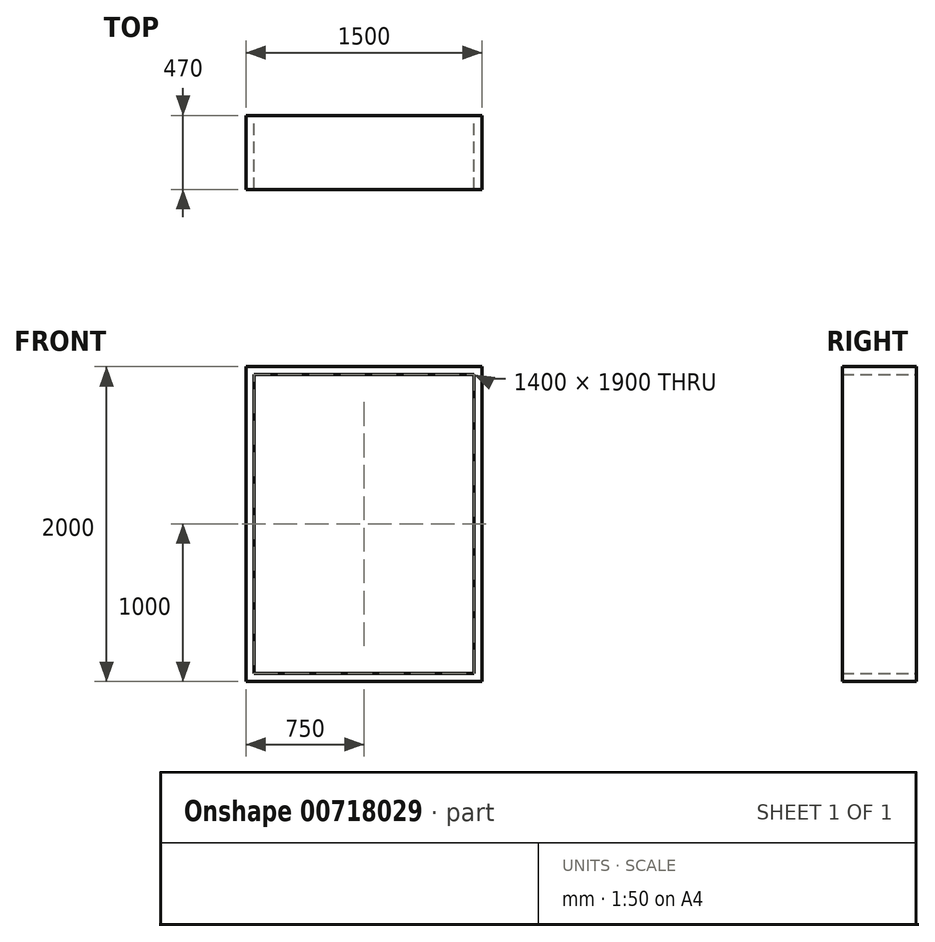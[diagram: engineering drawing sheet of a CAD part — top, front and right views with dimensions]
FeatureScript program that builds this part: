
annotation { "Feature Type Name" : "Feature", "Feature Type Description" : "" }
export const myFeature = defineFeature(function(context is Context, id is Id, definition is map)
    precondition{}
    {
        {
            var Q0;
            Q0=qCreatedBy(makeId("Front.planeOp"),FACE);
            var sketch = newSketch(context, id + "F0", { "sketchPlane" : qUnion([Q0])});
            skLineSegment(sketch, "E0.bottom", {"start": v(750, 1000) * mm, "end": v(-750, 1000) * mm});
            skLineSegment(sketch, "E0.top", {"start": v(750, -1000) * mm, "end": v(-750, -1000) * mm});
            skLineSegment(sketch, "E0.left", {"start": v(750, 1000) * mm, "end": v(750, -1000) * mm});
            skLineSegment(sketch, "E0.right", {"start": v(-750, 1000) * mm, "end": v(-750, -1000) * mm});
            skPoint(sketch, "E0.middle", {"position": v(0, 0) * mm});
            skLineSegment(sketch, "E1.0", {"start": v(700, 950) * mm, "end": v(-700, 950) * mm});
            skLineSegment(sketch, "E1.1", {"start": v(700, 950) * mm, "end": v(700, -950) * mm});
            skLineSegment(sketch, "E1.2", {"start": v(700, -950) * mm, "end": v(-700, -950) * mm});
            skLineSegment(sketch, "E1.3", {"start": v(-700, 950) * mm, "end": v(-700, -950) * mm});
            skSolve(sketch);
        }
        {
            var Q0;
            Q0=qSketchRegion(id+"F0",true);
            extrude(context, id + "F1", {"entities" : qUnion([Q0]), "depth" : 470 * mm, "offsetDistance" : 25 * mm});
        }
    });
